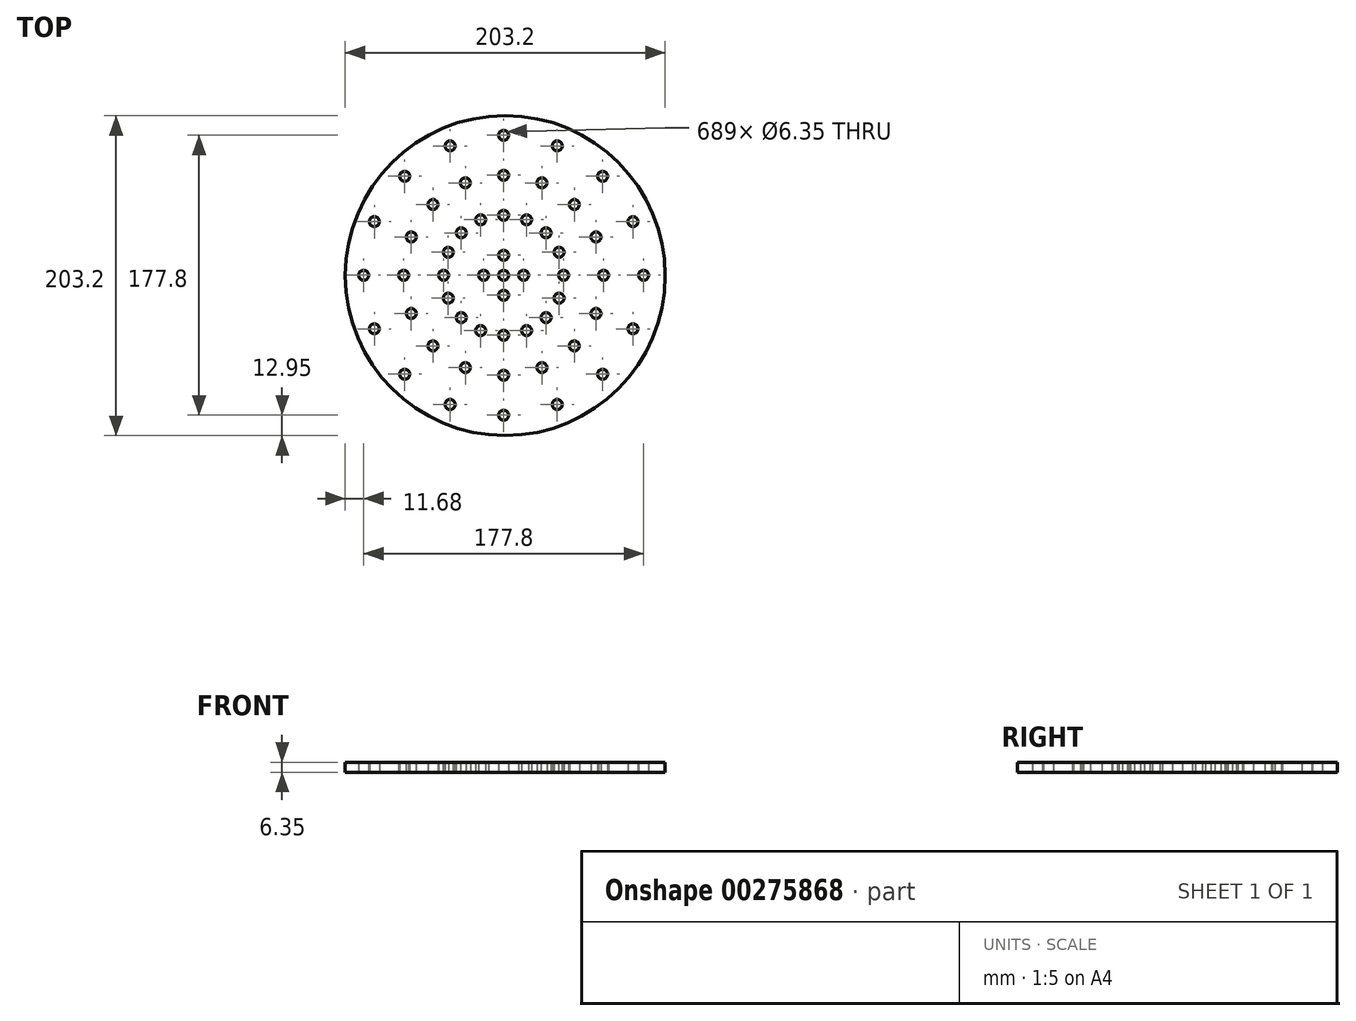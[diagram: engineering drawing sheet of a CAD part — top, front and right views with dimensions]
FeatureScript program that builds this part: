
annotation { "Feature Type Name" : "Feature", "Feature Type Description" : "" }
export const myFeature = defineFeature(function(context is Context, id is Id, definition is map)
    precondition{}
    {
        {
            var Q0;
            Q0=qCreatedBy(makeId("Top.planeOp"),FACE);
            var sketch = newSketch(context, id + "F0", { "sketchPlane" : qUnion([Q0])});
            skCircle(sketch, "E0", {"center": v(1.02, -0.25) * mm, "radius": 101.6 * mm});
            skLineSegment(sketch, "E1", {"start": v(0, 0) * mm, "end": v(0, 101.34) * mm, "construction": true});
            skPoint(sketch, "E2", {"position": v(0, 12.7) * mm});
            skCircle(sketch, "E3", {"center": v(0, 12.7) * mm, "radius": 3.18 * mm});
            skCircle(sketch, "E4.0.1.0", {"center": v(0, 38.1) * mm, "radius": 3.18 * mm});
            skCircle(sketch, "E4.0.2.0", {"center": v(0, 63.5) * mm, "radius": 3.18 * mm});
            skCircle(sketch, "E4.0.3.0", {"center": v(0, 88.9) * mm, "radius": 3.18 * mm});
            skLineSegment(sketch, "E4.direction1", {"start": v(0, 25.4) * mm, "end": v(25.4, 25.4) * mm, "construction": true});
            skLineSegment(sketch, "E4.direction2", {"start": v(0, 25.4) * mm, "end": v(0, 50.8) * mm, "construction": true});
            skCircle(sketch, "E5", {"center": v(0, 0) * mm, "radius": 3.18 * mm});
            skCircle(sketch, "E6.1.0", {"center": v(-14.58, 35.2) * mm, "radius": 3.18 * mm});
            skCircle(sketch, "E6.1.1", {"center": v(-24.3, 58.67) * mm, "radius": 3.18 * mm});
            skCircle(sketch, "E6.1.2", {"center": v(-34.02, 82.13) * mm, "radius": 3.18 * mm});
            skCircle(sketch, "E6.2.0", {"center": v(-26.94, 26.94) * mm, "radius": 3.18 * mm});
            skCircle(sketch, "E6.2.1", {"center": v(-44.9, 44.9) * mm, "radius": 3.18 * mm});
            skCircle(sketch, "E6.2.2", {"center": v(-62.86, 62.86) * mm, "radius": 3.18 * mm});
            skCircle(sketch, "E6.3.0", {"center": v(-35.2, 14.58) * mm, "radius": 3.18 * mm});
            skCircle(sketch, "E6.3.1", {"center": v(-58.67, 24.3) * mm, "radius": 3.18 * mm});
            skCircle(sketch, "E6.3.2", {"center": v(-82.13, 34.02) * mm, "radius": 3.18 * mm});
            skCircle(sketch, "E6.4.0", {"center": v(-38.1, 0) * mm, "radius": 3.18 * mm});
            skCircle(sketch, "E6.4.1", {"center": v(-63.5, 0) * mm, "radius": 3.18 * mm});
            skCircle(sketch, "E6.4.2", {"center": v(-88.9, 0) * mm, "radius": 3.18 * mm});
            skCircle(sketch, "E6.5.0", {"center": v(-35.2, -14.58) * mm, "radius": 3.18 * mm});
            skCircle(sketch, "E6.5.1", {"center": v(-58.67, -24.3) * mm, "radius": 3.18 * mm});
            skCircle(sketch, "E6.5.2", {"center": v(-82.13, -34.02) * mm, "radius": 3.18 * mm});
            skCircle(sketch, "E6.6.0", {"center": v(-26.94, -26.94) * mm, "radius": 3.18 * mm});
            skCircle(sketch, "E6.6.1", {"center": v(-44.9, -44.9) * mm, "radius": 3.18 * mm});
            skCircle(sketch, "E6.6.2", {"center": v(-62.86, -62.86) * mm, "radius": 3.18 * mm});
            skCircle(sketch, "E6.7.0", {"center": v(-14.58, -35.2) * mm, "radius": 3.18 * mm});
            skCircle(sketch, "E6.7.1", {"center": v(-24.3, -58.67) * mm, "radius": 3.18 * mm});
            skCircle(sketch, "E6.7.2", {"center": v(-34.02, -82.13) * mm, "radius": 3.18 * mm});
            skCircle(sketch, "E6.8.0", {"center": v(0, -38.1) * mm, "radius": 3.18 * mm});
            skCircle(sketch, "E6.8.1", {"center": v(0, -63.5) * mm, "radius": 3.18 * mm});
            skCircle(sketch, "E6.8.2", {"center": v(0, -88.9) * mm, "radius": 3.18 * mm});
            skCircle(sketch, "E6.9.0", {"center": v(14.58, -35.2) * mm, "radius": 3.18 * mm});
            skCircle(sketch, "E6.9.1", {"center": v(24.3, -58.67) * mm, "radius": 3.18 * mm});
            skCircle(sketch, "E6.9.2", {"center": v(34.02, -82.13) * mm, "radius": 3.18 * mm});
            skCircle(sketch, "E6.10.0", {"center": v(26.94, -26.94) * mm, "radius": 3.18 * mm});
            skCircle(sketch, "E6.10.1", {"center": v(44.9, -44.9) * mm, "radius": 3.18 * mm});
            skCircle(sketch, "E6.10.2", {"center": v(62.86, -62.86) * mm, "radius": 3.18 * mm});
            skCircle(sketch, "E6.11.0", {"center": v(35.2, -14.58) * mm, "radius": 3.18 * mm});
            skCircle(sketch, "E6.11.1", {"center": v(58.67, -24.3) * mm, "radius": 3.18 * mm});
            skCircle(sketch, "E6.11.2", {"center": v(82.13, -34.02) * mm, "radius": 3.18 * mm});
            skCircle(sketch, "E6.12.0", {"center": v(38.1, 0) * mm, "radius": 3.18 * mm});
            skCircle(sketch, "E6.12.1", {"center": v(63.5, 0) * mm, "radius": 3.18 * mm});
            skCircle(sketch, "E6.12.2", {"center": v(88.9, 0) * mm, "radius": 3.18 * mm});
            skCircle(sketch, "E6.13.0", {"center": v(35.2, 14.58) * mm, "radius": 3.18 * mm});
            skCircle(sketch, "E6.13.1", {"center": v(58.67, 24.3) * mm, "radius": 3.18 * mm});
            skCircle(sketch, "E6.13.2", {"center": v(82.13, 34.02) * mm, "radius": 3.18 * mm});
            skCircle(sketch, "E6.14.0", {"center": v(26.94, 26.94) * mm, "radius": 3.18 * mm});
            skCircle(sketch, "E6.14.1", {"center": v(44.9, 44.9) * mm, "radius": 3.18 * mm});
            skCircle(sketch, "E6.14.2", {"center": v(62.86, 62.86) * mm, "radius": 3.18 * mm});
            skCircle(sketch, "E6.15.0", {"center": v(14.58, 35.2) * mm, "radius": 3.18 * mm});
            skCircle(sketch, "E6.15.1", {"center": v(24.3, 58.67) * mm, "radius": 3.18 * mm});
            skCircle(sketch, "E6.15.2", {"center": v(34.02, 82.13) * mm, "radius": 3.18 * mm});
            skCircle(sketch, "E7.2.0", {"center": v(-12.7, 0) * mm, "radius": 3.18 * mm});
            skCircle(sketch, "E7.4.0", {"center": v(0, -12.7) * mm, "radius": 3.18 * mm});
            skCircle(sketch, "E7.6.0", {"center": v(12.7, 0) * mm, "radius": 3.18 * mm});
            skSolve(sketch);
        }
        {
            var Q0;
            Q0=makeQuery(id+"F0.imprint","IMPRINT",FACE,{"disambiguationData":[TD([[makeQuery(id+"F0.imprint","IMPRINT",EDGE,{"derivedFrom":sQuery(id+"F0.wireOp",EDGE,"E0")}),1.0]])]});
            extrude(context, id + "F1", {"entities" : qUnion([Q0]), "depth" : 6.35 * mm});
        }
        {
            var Q0;
            Q0=sQuery(id+"F0.wireOp",EDGE,"E5");
            extrude(context, id + "F2", {"bodyType" : ToolBodyType.SURFACE, "surfaceEntities" : qUnion([Q0]), "depth" : 123.7 * mm, "hasSecondDirection" : true, "secondDirectionOppositeDirection" : true, "secondDirectionDepth" : 40.9 * mm});
        }
    });
